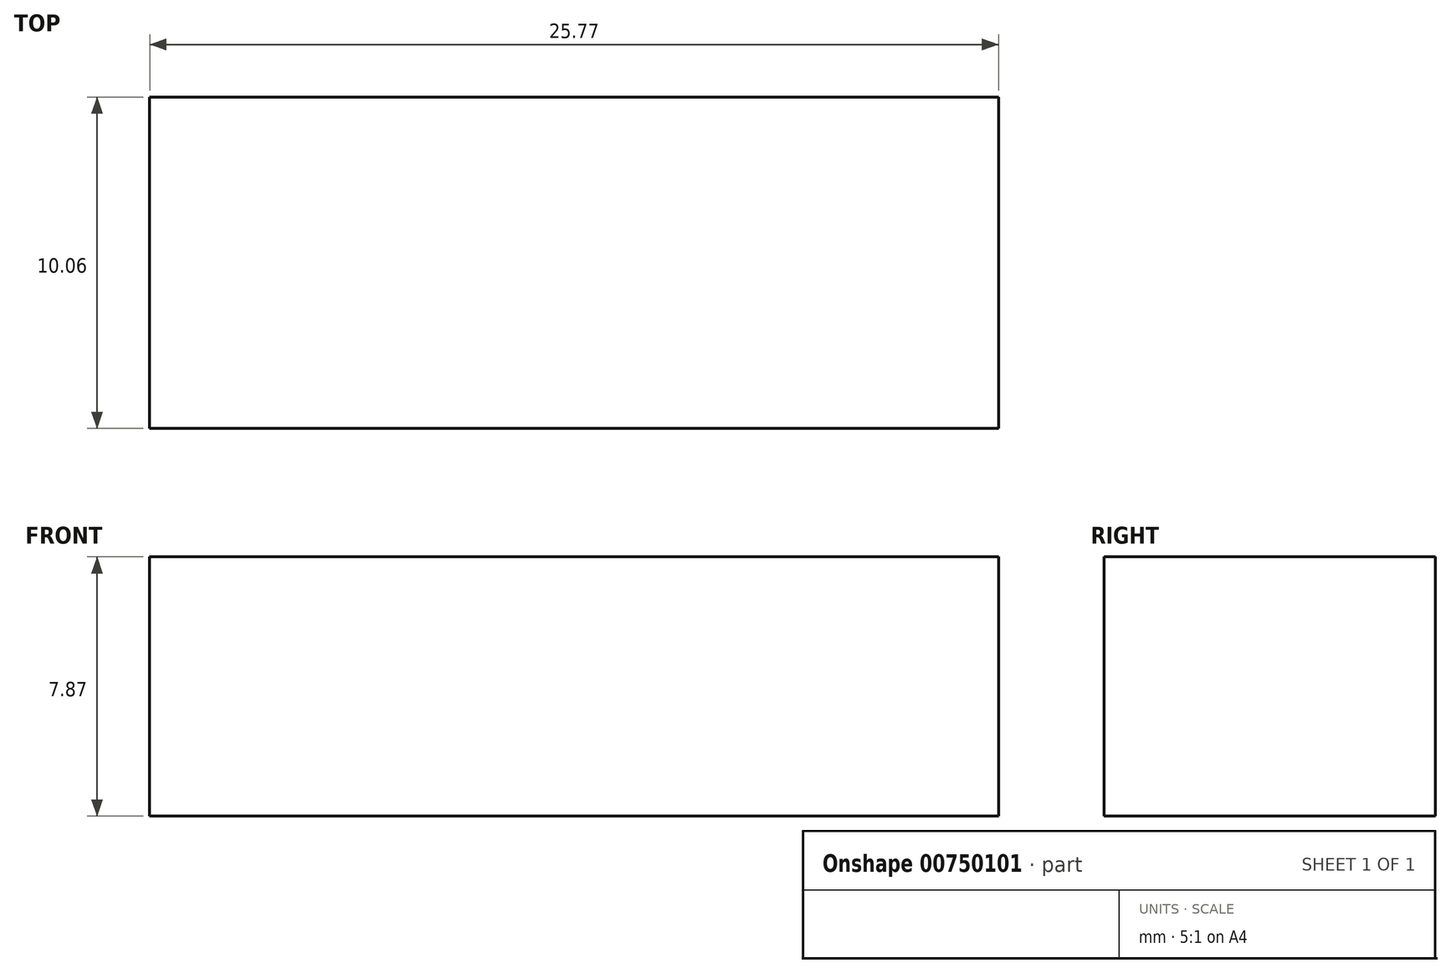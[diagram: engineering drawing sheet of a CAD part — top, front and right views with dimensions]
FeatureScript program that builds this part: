
annotation { "Feature Type Name" : "Feature", "Feature Type Description" : "" }
export const myFeature = defineFeature(function(context is Context, id is Id, definition is map)
    precondition{}
    {
        {
            var Q0;
            Q0=qCreatedBy(makeId("Top.planeOp"),FACE);
            var sketch = newSketch(context, id + "F0", { "sketchPlane" : qUnion([Q0])});
            skLineSegment(sketch, "E0.bottom", {"start": v(-31.97, 18.1) * mm, "end": v(-6.2, 18.1) * mm});
            skLineSegment(sketch, "E0.top", {"start": v(-31.97, 8.03) * mm, "end": v(-6.2, 8.03) * mm});
            skLineSegment(sketch, "E0.left", {"start": v(-31.97, 18.1) * mm, "end": v(-31.97, 8.03) * mm});
            skLineSegment(sketch, "E0.right", {"start": v(-6.2, 18.1) * mm, "end": v(-6.2, 8.03) * mm});
            skSolve(sketch);
        }
        {
            var Q0;
            Q0 = qSketchRegion(id + "F0", true);
            extrude(context, id + "F1", {"entities" : qUnion([Q0]), "depth" : 7.87 * mm, "offsetDistance" : 25.4 * mm});
        }
    });
